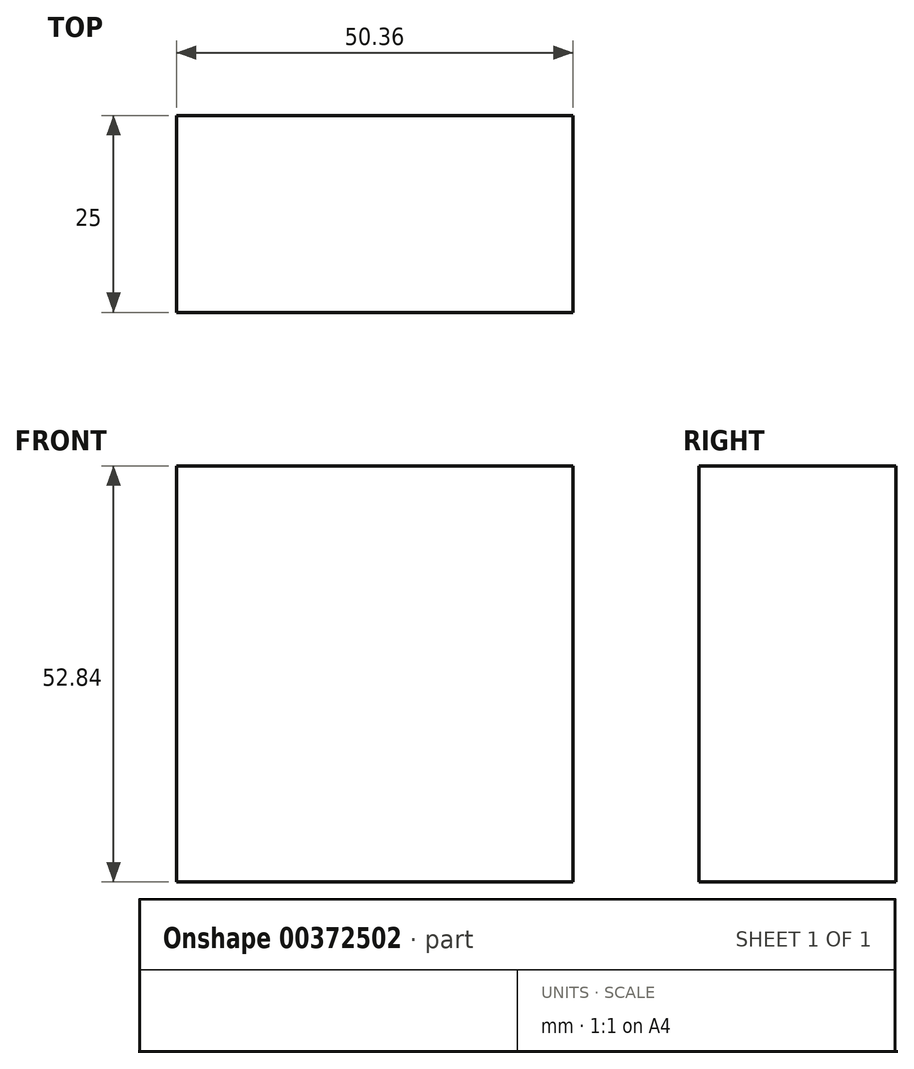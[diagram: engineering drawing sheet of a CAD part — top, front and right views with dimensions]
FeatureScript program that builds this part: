
annotation { "Feature Type Name" : "Feature", "Feature Type Description" : "" }
export const myFeature = defineFeature(function(context is Context, id is Id, definition is map)
    precondition{}
    {
        {
            var Q0;
            Q0=qCreatedBy(makeId("Front.planeOp"),FACE);
            var sketch = newSketch(context, id + "F0", { "sketchPlane" : qUnion([Q0])});
            skLineSegment(sketch, "E0.bottom", {"start": v(-229.34, -6.43) * mm, "end": v(-178.98, -6.43) * mm});
            skLineSegment(sketch, "E0.top", {"start": v(-229.34, 46.4) * mm, "end": v(-178.98, 46.4) * mm});
            skLineSegment(sketch, "E0.left", {"start": v(-229.34, -6.43) * mm, "end": v(-229.34, 46.4) * mm});
            skLineSegment(sketch, "E0.right", {"start": v(-178.98, -6.43) * mm, "end": v(-178.98, 46.4) * mm});
            skPoint(sketch, "E0.middle", {"position": v(-204.16, 19.99) * mm});
            skSolve(sketch);
        }
        {
            var Q0;
            Q0=makeQuery(id+"F0.imprint","IMPRINT",FACE,{"disambiguationData":[TD([[makeQuery(id+"F0.imprint","IMPRINT",EDGE,{"derivedFrom":sQuery(id+"F0.wireOp",EDGE,"E0.bottom")}),1.0]])]});
            extrude(context, id + "F1", {"entities" : qUnion([Q0]), "depth" : 25 * mm});
        }
    });
